# Revit family: BIM_Model_Piranhamat_ 100_60_L
name_source: partatom
category: Mechanical Equipment
revit_build: Autodesk Revit 2018 (Build: 20170223_1515(x64)
units: mm (PartAtom-declared; Revit-internal decimal feet)

## family parameters
Always vertical = Yes
Cut with Voids When Loaded = No
Part Type = Normal
Room Calculation Point = No
Round Connector Dimension = Use Radius
Shared = No
Work Plane-Based = No

## types (2) — shared parameters
Cable Length (m) = 2.2
Cable Type (H05V V-F) = 3G1.0
Capacity (m3/hr) = 5.8 m³
Description = Compact fecal pumping units for direct connection of one toilet in accordance with EN 12050-3. These ready-to-plug-in units, with a gas- and odor-tight synthetic tank, can also be connected to a hand wash basin, shower, or bidet.
Discharge DN25/32 = 16 mm  [stored 0.0524934 ft]
Head (m) = 8 mm  [stored 0.0262467 ft]
Inflow DN 100 = 50 mm  [stored 0.164042 ft]
Inflow DN 40 = 20 mm  [stored 0.0656168 ft]
Manufacturer = Sulzer
Model = Piranhamat
Motor Power (kW) = P1=1.10 P2=0.68
Product Specification Link = https://www.sulzer.com
Rated Current (A) = 4.84
Rated Voltage (V) = 220-240 1~
Speed (r/min) = 2900
Tank Material = Polypropylene
Weight (Kg) = 9.0

## per-type parameters (varying)
| type | Connection Height Offset | Connection Offset (Horizontal) |
| Piranhamat 100 Connection @ 74mm Height | 74 mm  [stored 0.242782 ft] | 42 mm  [stored 0.137795 ft] |
| Piranhamat 100 Connection @ 198mm Height | 198 mm  [stored 0.649606 ft] | 36 mm  [stored 0.11811 ft] |

note: [stored X ft] marks values corroborated as IEEE doubles in the binary element streams (Revit-internal decimal feet)

## geometry (parser evidence)
native form markers: Sweep x3
no freeform markers — native parametric forms only
